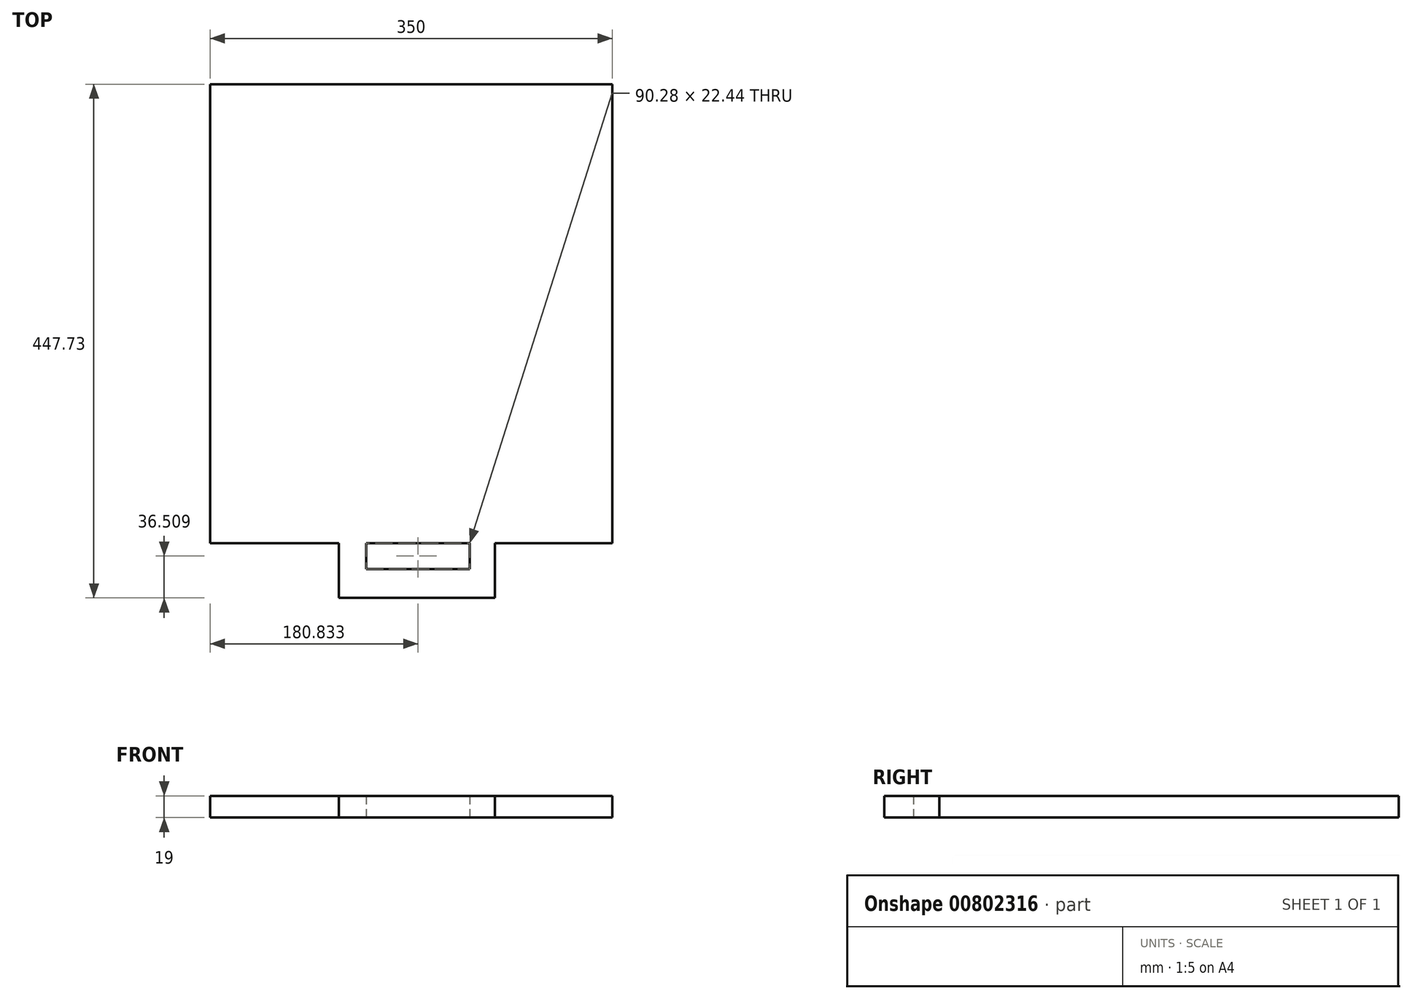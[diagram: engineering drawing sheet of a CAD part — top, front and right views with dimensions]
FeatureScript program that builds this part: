
annotation { "Feature Type Name" : "Feature", "Feature Type Description" : "" }
export const myFeature = defineFeature(function(context is Context, id is Id, definition is map)
    precondition{}
    {
        {
            var Q0;
            Q0=qCreatedBy(makeId("Top.planeOp"),FACE);
            var sketch = newSketch(context, id + "F0", { "sketchPlane" : qUnion([Q0])});
            skLineSegment(sketch, "E0.bottom", {"start": v(175, 200) * mm, "end": v(-175, 200) * mm});
            skLineSegment(sketch, "E0.top", {"start": v(175, -200) * mm, "end": v(-175, -200) * mm});
            skLineSegment(sketch, "E0.left", {"start": v(175, 200) * mm, "end": v(175, -200) * mm});
            skLineSegment(sketch, "E0.right", {"start": v(-175, 200) * mm, "end": v(-175, -200) * mm});
            skPoint(sketch, "E0.middle", {"position": v(0, 0) * mm});
            skLineSegment(sketch, "E1.bottom", {"start": v(-63.01, -200) * mm, "end": v(72.85, -200) * mm});
            skLineSegment(sketch, "E1.top", {"start": v(-63.01, -247.73) * mm, "end": v(72.85, -247.73) * mm});
            skLineSegment(sketch, "E1.left", {"start": v(-63.01, -200) * mm, "end": v(-63.01, -247.73) * mm});
            skLineSegment(sketch, "E1.right", {"start": v(72.85, -200) * mm, "end": v(72.85, -247.73) * mm});
            skLineSegment(sketch, "E2.bottom", {"start": v(-39.3, -200) * mm, "end": v(50.97, -200) * mm});
            skLineSegment(sketch, "E2.top", {"start": v(-39.3, -222.44) * mm, "end": v(50.97, -222.44) * mm});
            skLineSegment(sketch, "E2.left", {"start": v(-39.3, -200) * mm, "end": v(-39.3, -222.44) * mm});
            skLineSegment(sketch, "E2.right", {"start": v(50.97, -200) * mm, "end": v(50.97, -222.44) * mm});
            skSolve(sketch);
        }
        {
            var Q0;
            Q0=makeQuery(id+"F0.imprint","IMPRINT",FACE,{"disambiguationData":[TD([[makeQuery(id+"F0.imprint","IMPRINT",EDGE,{"derivedFrom":sQuery(id+"F0.wireOp",EDGE,"E0.bottom")}),1.0]])]});
            var Q1;
            Q1=makeQuery(id+"F0.imprint","IMPRINT",FACE,{"disambiguationData":[TD([[makeQuery(id+"F0.imprint","IMPRINT",EDGE,{"derivedFrom":sQuery(id+"F0.wireOp",EDGE,"E1.top")}),1.0]])]});
            extrude(context, id + "F1", {"entities" : qUnion([Q0, Q1]), "depth" : 19 * mm, "offsetDistance" : 25 * mm});
        }
    });
